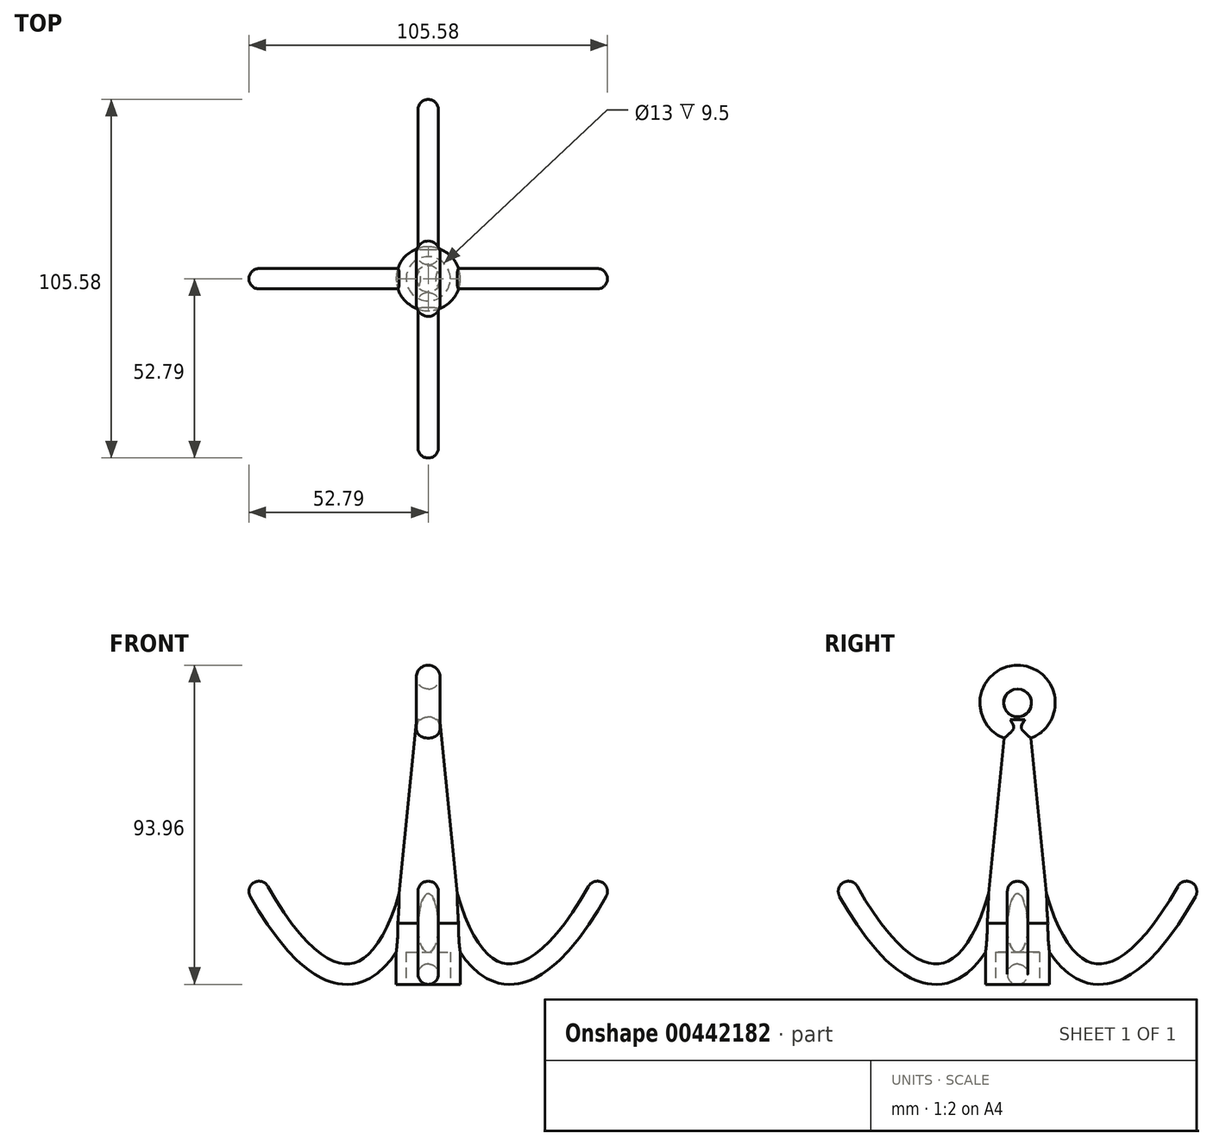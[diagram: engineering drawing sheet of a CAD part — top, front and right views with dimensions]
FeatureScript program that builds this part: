
annotation { "Feature Type Name" : "Feature", "Feature Type Description" : "" }
export const myFeature = defineFeature(function(context is Context, id is Id, definition is map)
    precondition{}
    {
        {
            var Q0;
            Q0=qCreatedBy(makeId("Front.planeOp"),FACE);
            var sketch = newSketch(context, id + "F0", { "sketchPlane" : qUnion([Q0])});
            skFitSpline(sketch, "E0", {"points": [v(0, 0) * mm, v(49.8, -50.6) * mm], "startDerivative": vector(0, -219.16) * mm, "endDerivative": vector(80.33, 143.22) * mm});
            skSolve(sketch);
        }
        {
            var Q0;
            Q0=qCreatedBy(makeId("Top.planeOp"),FACE);
            var sketch = newSketch(context, id + "F1", { "sketchPlane" : qUnion([Q0])});
            skCircle(sketch, "E1", {"center": v(0, 0) * mm, "radius": 3 * mm});
            skSolve(sketch);
        }
        {
            var Q0;
            Q0 = qSketchRegion(id + "F1", true);
            var Q1;
            Q1=sQuery(id+"F1.wireOp",EDGE,"E1");
            var Q2;
            Q2=sQuery(id+"F0.wireOp",EDGE,"E0");
            sweep(context, id + "F2", {"profiles" : qUnion([Q0]), "surfaceProfiles" : qUnion([Q1]), "path" : qUnion([Q2])});
        }
        {
            var Q0;
            Q0=qCreatedBy(makeId("Front.planeOp"),FACE);
            var sketch = newSketch(context, id + "F3", { "sketchPlane" : qUnion([Q0])});
            skArc(sketch, "E2", {"start": v(52.4, -52.06) * mm, "mid": v(48.32, -53.21) * mm, "end": v(47.18, -49.13) * mm});
            skLineSegment(sketch, "E3", {"start": v(47.18, -49.13) * mm, "end": v(52.4, -52.06) * mm});
            skSolve(sketch);
        }
        {
            var Q0;
            Q0 = qSketchRegion(id + "F3", true);
            var Q1;
            Q1=sQuery(id+"F3.wireOp",EDGE,"E2");
            var Q2;
            Q2=sQuery(id+"F3.wireOp",EDGE,"E3");
            revolve(context, id + "F4", {"operationType" : NewBodyOperationType.ADD, "entities" : qUnion([Q0]), "surfaceEntities" : qUnion([Q1]), "axis" : qUnion([Q2]), "revolveType" : RevolveType.FULL});
        }
        {
            var Q0;
            Q0=qCreatedBy(makeId("Front.planeOp"),FACE);
            var sketch = newSketch(context, id + "F5", { "sketchPlane" : qUnion([Q0])});
            skLineSegment(sketch, "E4", {"start": v(0, 0) * mm, "end": v(0, -75.3) * mm});
            skSolve(sketch);
        }
        {
            var Q0;
            Q0=makeQuery(id+"F2.opSweep","SWEPT_BODY",BODY,{"disambiguationData":[OSD([sQuery(id+"F0.wireOp",EDGE,"E0"),sQuery(id+"F1.wireOp",EDGE,"E1")])]});
            var Q1;
            Q1=sQuery(id+"F5.wireOp",EDGE,"E4");
            circularPattern(context, id + "F6", {"operationType" : NewBodyOperationType.ADD, "entities" : qUnion([Q0]), "axis" : qUnion([Q1]), "angle" : 360 * degree, "instanceCount" : 4, "equalSpace" : true});
        }
        {
            var Q0;
            Q0=qCreatedBy(makeId("Top.planeOp"),FACE);
            cPlane(context, id + "F7", {"entities" : qUnion([Q0]), "cplaneType" : CPlaneType.OFFSET, "offset" : 77.97 * mm, "oppositeDirection" : true, "width" : 150 * mm, "height" : 150 * mm});
        }
        {
            var Q0;
            Q0=qCreatedBy(id+"F7.planeOp",FACE);
            var sketch = newSketch(context, id + "F8", { "sketchPlane" : qUnion([Q0])});
            skCircle(sketch, "E5.0", {"center": v(0, 0) * mm, "radius": 9.43 * mm});
            skSolve(sketch);
        }
        {
            var Q0;
            Q0 = qSketchRegion(id + "F8", true);
            extrude(context, id + "F9", {"entities" : qUnion([Q0]), "operationType" : NewBodyOperationType.ADD, "depth" : 77.97 * mm});
        }
        {
            var Q0;
            Q0=makeQuery(id+"F9.opExtrude","CAP_FACE",FACE,{"disambiguationData":[OSD([sQuery(id+"F8.wireOp",EDGE,"E5.0")])],"isStart":true});
            var sketch = newSketch(context, id + "F10", { "sketchPlane" : qUnion([Q0])});
            skCircle(sketch, "E6", {"center": v(0, 0) * mm, "radius": 6.5 * mm});
            skSolve(sketch);
        }
        {
            var Q0;
            Q0 = qSketchRegion(id + "F10", true);
            extrude(context, id + "F11", {"entities" : qUnion([Q0]), "operationType" : NewBodyOperationType.REMOVE, "oppositeDirection" : true, "depth" : 9.5 * mm});
        }
        {
            var Q0;
            Q0=makeQuery(id+"F9.opExtrude","CAP_EDGE",EDGE,{"disambiguationData":[OSD([sQuery(id+"F8.wireOp",EDGE,"E5.0")])],"isStart":false});
            chamfer(context, id + "F12", {"entities" : qUnion([Q0]), "chamferType" : ChamferType.TWO_OFFSETS, "width1" : 6 * mm, "oppositeDirection" : false, "width2" : 60 * mm, "tangentPropagation" : true});
        }
        {
            var Q0;
            Q0=qCreatedBy(makeId("Right.planeOp"),FACE);
            var sketch = newSketch(context, id + "F13", { "sketchPlane" : qUnion([Q0])});
            skCircle(sketch, "E7", {"center": v(0, 4.9) * mm, "radius": 6 * mm});
            skSolve(sketch);
        }
        {
            var Q0;
            Q0=qCreatedBy(makeId("Front.planeOp"),FACE);
            var sketch = newSketch(context, id + "F14", { "sketchPlane" : qUnion([Q0])});
            skCircle(sketch, "E8", {"center": v(0, 12.5) * mm, "radius": 3.5 * mm});
            skSolve(sketch);
        }
        {
            var Q0;
            Q0=makeQuery(id+"F14.imprint","IMPRINT",FACE,{"disambiguationData":[TD([[makeQuery(id+"F14.imprint","IMPRINT",EDGE,{"derivedFrom":sQuery(id+"F14.wireOp",EDGE,"E8")}),1.0]])]});
            var Q1;
            Q1=sQuery(id+"F13.wireOp",EDGE,"E7");
            revolve(context, id + "F15", {"operationType" : NewBodyOperationType.ADD, "entities" : qUnion([Q0]), "axis" : qUnion([Q1]), "revolveType" : RevolveType.FULL});
        }
    });
